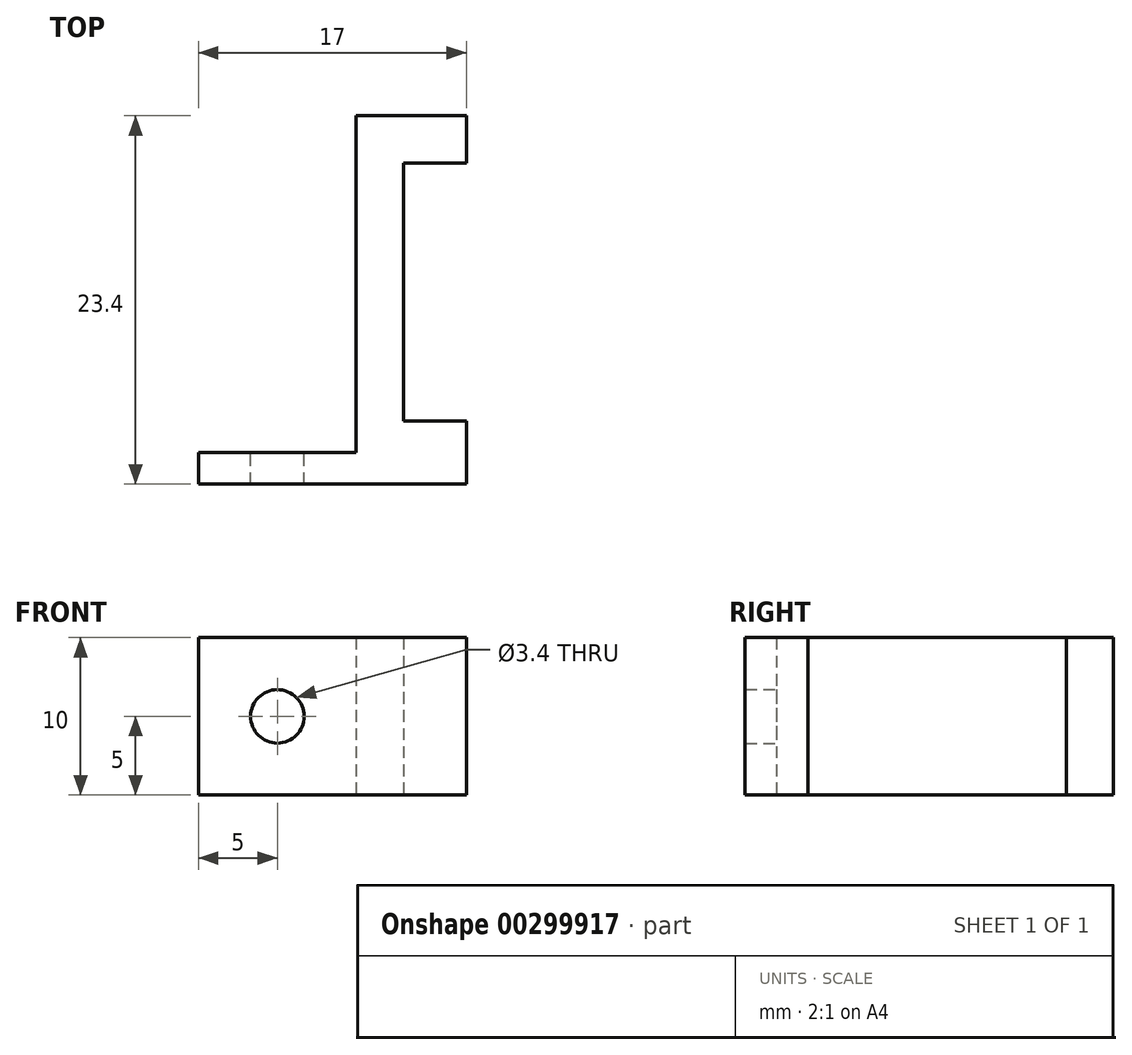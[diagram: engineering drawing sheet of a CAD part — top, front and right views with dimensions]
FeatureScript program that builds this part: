
annotation { "Feature Type Name" : "Feature", "Feature Type Description" : "" }
export const myFeature = defineFeature(function(context is Context, id is Id, definition is map)
    precondition{}
    {
        {
            var Q0;
            Q0=qCreatedBy(makeId("Top.planeOp"),FACE);
            var sketch = newSketch(context, id + "F0", { "sketchPlane" : qUnion([Q0])});
            skLineSegment(sketch, "E0", {"start": v(0, 0) * mm, "end": v(0, 2) * mm});
            skLineSegment(sketch, "E1", {"start": v(0, 2) * mm, "end": v(10, 2) * mm});
            skLineSegment(sketch, "E2", {"start": v(10, 2) * mm, "end": v(10, 23.4) * mm});
            skLineSegment(sketch, "E3", {"start": v(10, 23.4) * mm, "end": v(17, 23.4) * mm});
            skLineSegment(sketch, "E4", {"start": v(17, 23.4) * mm, "end": v(17, 20.4) * mm});
            skLineSegment(sketch, "E5", {"start": v(17, 20.4) * mm, "end": v(13, 20.4) * mm});
            skLineSegment(sketch, "E6", {"start": v(13, 20.4) * mm, "end": v(13, 4) * mm});
            skLineSegment(sketch, "E7", {"start": v(13, 4) * mm, "end": v(17, 4) * mm});
            skLineSegment(sketch, "E8", {"start": v(17, 4) * mm, "end": v(17, 0) * mm});
            skLineSegment(sketch, "E9", {"start": v(17, 0) * mm, "end": v(0, 0) * mm});
            skLineSegment(sketch, "E10", {"start": v(17, 4) * mm, "end": v(17, 20.4) * mm, "construction": true});
            skSolve(sketch);
        }
        {
            var Q0;
            Q0 = qSketchRegion(id + "F0", true);
            extrude(context, id + "F1", {"entities" : qUnion([Q0]), "depth" : 10 * mm});
        }
        {
            var Q0;
            Q0=makeQuery(id+"F1.opExtrude","SWEPT_FACE",FACE,{"disambiguationData":[OSD([sQuery(id+"F0.wireOp",EDGE,"E1")])]});
            var sketch = newSketch(context, id + "F2", { "sketchPlane" : qUnion([Q0])});
            skCircle(sketch, "E11", {"center": v(-5, 5) * mm, "radius": 1.7 * mm});
            skPoint(sketch, "E11.centerSnap0", {"position": v(0, 5) * mm});
            skPoint(sketch, "E11.centerSnap1", {"position": v(-5, 10) * mm});
            skSolve(sketch);
        }
        {
            var Q0;
            Q0=makeQuery(id+"F2.imprint","IMPRINT",FACE,{"disambiguationData":[TD([[makeQuery(id+"F2.imprint","IMPRINT",EDGE,{"derivedFrom":sQuery(id+"F2.wireOp",EDGE,"E11")}),1.0]])]});
            extrude(context, id + "F3", {"entities" : qUnion([Q0]), "operationType" : NewBodyOperationType.REMOVE, "oppositeDirection" : true, "depth" : 25 * mm});
        }
    });
